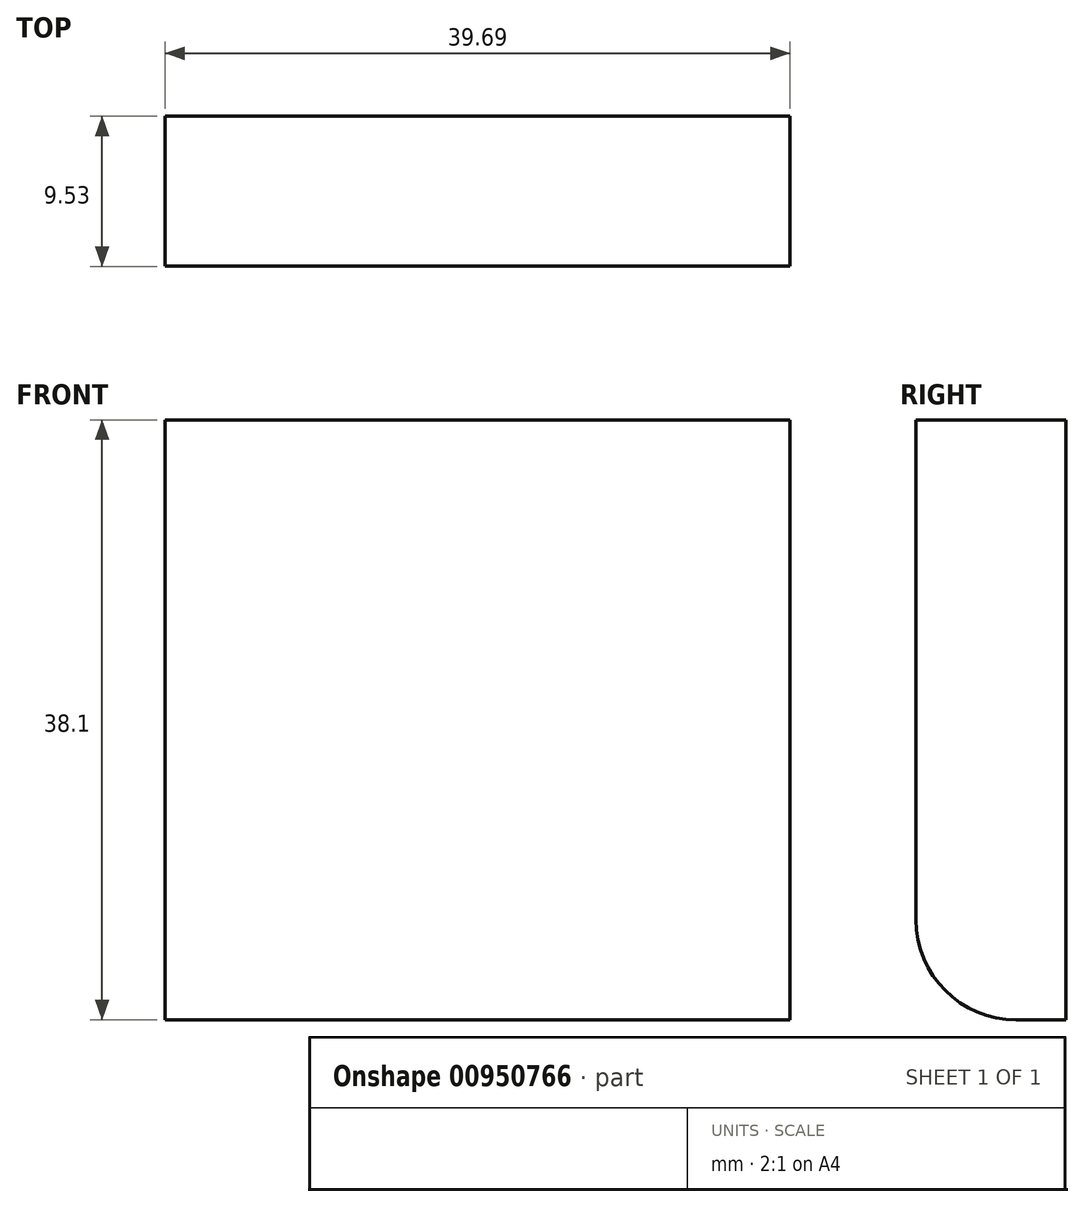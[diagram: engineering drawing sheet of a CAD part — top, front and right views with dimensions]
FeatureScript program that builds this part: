
annotation { "Feature Type Name" : "Feature", "Feature Type Description" : "" }
export const myFeature = defineFeature(function(context is Context, id is Id, definition is map)
    precondition{}
    {
        {
            var Q0;
            Q0=qCreatedBy(makeId("Front.planeOp"),FACE);
            var sketch = newSketch(context, id + "F0", { "sketchPlane" : qUnion([Q0])});
            skLineSegment(sketch, "E0.bottom", {"start": v(-16.5, 12.8) * mm, "end": v(23.19, 12.8) * mm});
            skLineSegment(sketch, "E0.top", {"start": v(-16.5, -25.3) * mm, "end": v(23.19, -25.3) * mm});
            skLineSegment(sketch, "E0.left", {"start": v(-16.5, 12.8) * mm, "end": v(-16.5, -25.3) * mm});
            skLineSegment(sketch, "E0.right", {"start": v(23.19, 12.8) * mm, "end": v(23.19, -25.3) * mm});
            skSolve(sketch);
        }
        {
            var Q0;
            Q0=makeQuery(id+"F0.imprint","IMPRINT",FACE,{"disambiguationData":[TD([[makeQuery(id+"F0.imprint","IMPRINT",EDGE,{"derivedFrom":sQuery(id+"F0.wireOp",EDGE,"E0.bottom")}),-1.0]])]});
            extrude(context, id + "F1", {"entities" : qUnion([Q0]), "depth" : 9.52 * mm, "offsetDistance" : 25.4 * mm});
        }
        {
            var Q0;
            Q0=makeQuery(id+"F1.opExtrude","CAP_EDGE",EDGE,{"disambiguationData":[OSD([sQuery(id+"F0.wireOp",EDGE,"E0.top")])],"isStart":false});
            fillet(context, id + "F2", {"entities" : qUnion([Q0]), "radius" : 6.35 * mm, "tangentPropagation" : true, "allowEdgeOverflow" : false});
        }
    });
